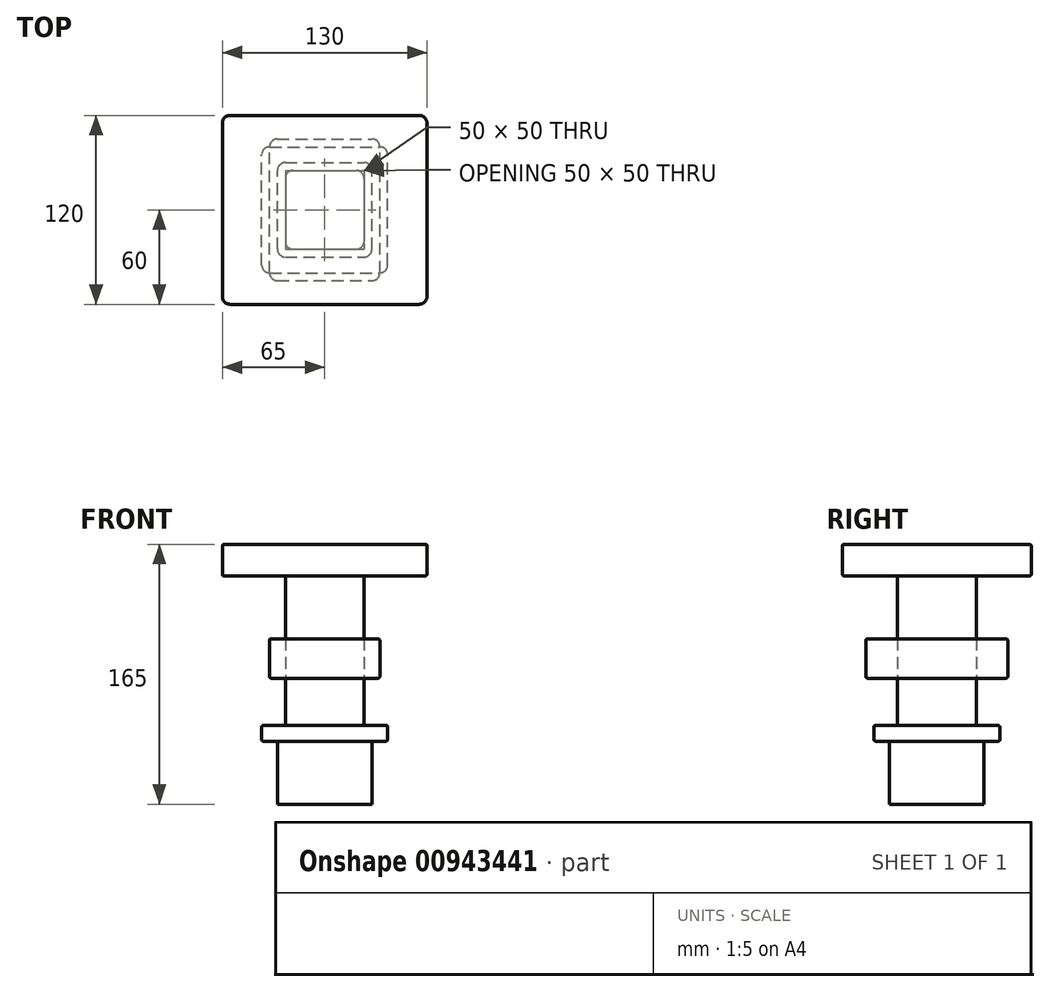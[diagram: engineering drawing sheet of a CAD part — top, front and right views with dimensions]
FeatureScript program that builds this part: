
annotation { "Feature Type Name" : "Feature", "Feature Type Description" : "" }
export const myFeature = defineFeature(function(context is Context, id is Id, definition is map)
    precondition{}
    {
        {
            var Q0;
            Q0=qCreatedBy(makeId("Top.planeOp"),FACE);
            var sketch = newSketch(context, id + "F0", { "sketchPlane" : qUnion([Q0])});
            skLineSegment(sketch, "E0.bottom", {"start": v(-30, -30) * mm, "end": v(30, -30) * mm});
            skLineSegment(sketch, "E0.top", {"start": v(-30, 30) * mm, "end": v(30, 30) * mm});
            skLineSegment(sketch, "E0.left", {"start": v(-30, -30) * mm, "end": v(-30, 30) * mm});
            skLineSegment(sketch, "E0.right", {"start": v(30, -30) * mm, "end": v(30, 30) * mm});
            skPoint(sketch, "E0.middle", {"position": v(0, 0) * mm});
            skSolve(sketch);
        }
        {
            var Q0;
            Q0=makeQuery(id+"F0.imprint","IMPRINT",FACE,{"disambiguationData":[TD([[makeQuery(id+"F0.imprint","IMPRINT",EDGE,{"derivedFrom":sQuery(id+"F0.wireOp",EDGE,"E0.bottom")}),1.0]])]});
            extrude(context, id + "F1", {"entities" : qUnion([Q0]), "depth" : 40 * mm, "offsetDistance" : 25 * mm});
        }
        {
            var Q0;
            Q0=makeQuery(id+"F1.opExtrude","CAP_FACE",FACE,{"disambiguationData":[OSD([sQuery(id+"F0.wireOp",EDGE,"E0.bottom"),sQuery(id+"F0.wireOp",EDGE,"E0.top"),sQuery(id+"F0.wireOp",EDGE,"E0.left"),sQuery(id+"F0.wireOp",EDGE,"E0.right")])],"isStart":false});
            var sketch = newSketch(context, id + "F2", { "sketchPlane" : qUnion([Q0])});
            skLineSegment(sketch, "E1.bottom", {"start": v(-40, -40) * mm, "end": v(40, -40) * mm});
            skLineSegment(sketch, "E1.top", {"start": v(-40, 40) * mm, "end": v(40, 40) * mm});
            skLineSegment(sketch, "E1.left", {"start": v(-40, -40) * mm, "end": v(-40, 40) * mm});
            skLineSegment(sketch, "E1.right", {"start": v(40, -40) * mm, "end": v(40, 40) * mm});
            skPoint(sketch, "E1.middle", {"position": v(0, 0) * mm});
            skSolve(sketch);
        }
        {
            var Q0;
            Q0 = qSketchRegion(id + "F2", true);
            extrude(context, id + "F3", {"entities" : qUnion([Q0]), "operationType" : NewBodyOperationType.ADD, "depth" : 10 * mm, "offsetDistance" : 25 * mm});
        }
        {
            var Q0;
            Q0=makeQuery(id+"F3.opExtrude","CAP_FACE",FACE,{"disambiguationData":[OSD([sQuery(id+"F2.wireOp",EDGE,"E1.bottom"),sQuery(id+"F2.wireOp",EDGE,"E1.top"),sQuery(id+"F2.wireOp",EDGE,"E1.left"),sQuery(id+"F2.wireOp",EDGE,"E1.right")])],"isStart":false});
            var sketch = newSketch(context, id + "F4", { "sketchPlane" : qUnion([Q0])});
            skLineSegment(sketch, "E2.bottom", {"start": v(-25, 25) * mm, "end": v(25, 25) * mm});
            skLineSegment(sketch, "E2.top", {"start": v(-25, -25) * mm, "end": v(25, -25) * mm});
            skLineSegment(sketch, "E2.left", {"start": v(-25, 25) * mm, "end": v(-25, -25) * mm});
            skLineSegment(sketch, "E2.right", {"start": v(25, 25) * mm, "end": v(25, -25) * mm});
            skPoint(sketch, "E2.middle", {"position": v(0, 0) * mm});
            skSolve(sketch);
        }
        {
            var Q0;
            Q0=makeQuery(id+"F4.imprint","IMPRINT",FACE,{"disambiguationData":[TD([[makeQuery(id+"F4.imprint","IMPRINT",EDGE,{"derivedFrom":sQuery(id+"F4.wireOp",EDGE,"E2.bottom")}),-1.0]])]});
            extrude(context, id + "F5", {"entities" : qUnion([Q0]), "operationType" : NewBodyOperationType.ADD, "depth" : 30 * mm, "offsetDistance" : 25 * mm});
        }
        {
            var Q0;
            Q0=makeQuery(id+"F5.opExtrude","CAP_FACE",FACE,{"disambiguationData":[OSD([sQuery(id+"F4.wireOp",EDGE,"E2.bottom"),sQuery(id+"F4.wireOp",EDGE,"E2.top"),sQuery(id+"F4.wireOp",EDGE,"E2.left"),sQuery(id+"F4.wireOp",EDGE,"E2.right")])],"isStart":false});
            var sketch = newSketch(context, id + "F6", { "sketchPlane" : qUnion([Q0])});
            skLineSegment(sketch, "E3.bottom", {"start": v(-35, -45) * mm, "end": v(35, -45) * mm});
            skLineSegment(sketch, "E3.top", {"start": v(-35, 45) * mm, "end": v(35, 45) * mm});
            skLineSegment(sketch, "E3.left", {"start": v(-35, -45) * mm, "end": v(-35, 45) * mm});
            skLineSegment(sketch, "E3.right", {"start": v(35, -45) * mm, "end": v(35, 45) * mm});
            skPoint(sketch, "E3.middle", {"position": v(0, 0) * mm});
            skSolve(sketch);
        }
        {
            var Q0;
            Q0=makeQuery(id+"F6.imprint","IMPRINT",FACE,{"disambiguationData":[TD([[makeQuery(id+"F6.imprint","IMPRINT",EDGE,{"derivedFrom":sQuery(id+"F6.wireOp",EDGE,"E3.bottom")}),1.0]])]});
            extrude(context, id + "F7", {"entities" : qUnion([Q0]), "depth" : 25 * mm, "offsetDistance" : 25 * mm});
        }
        {
            var Q0;
            Q0=makeQuery(id+"F5.opExtrude","CAP_FACE",FACE,{"disambiguationData":[OSD([sQuery(id+"F4.wireOp",EDGE,"E2.bottom"),sQuery(id+"F4.wireOp",EDGE,"E2.top"),sQuery(id+"F4.wireOp",EDGE,"E2.left"),sQuery(id+"F4.wireOp",EDGE,"E2.right")])],"isStart":false});
            extrude(context, id + "F8", {"entities" : qUnion([Q0]), "depth" : 65 * mm, "offsetDistance" : 25 * mm});
        }
        {
            var Q0;
            Q0=makeQuery(id+"F8.opExtrude","CAP_FACE",FACE,{"disambiguationData":[OSD([sQuery(id+"F4.wireOp",EDGE,"E2.bottom"),sQuery(id+"F4.wireOp",EDGE,"E2.top"),sQuery(id+"F4.wireOp",EDGE,"E2.left"),sQuery(id+"F4.wireOp",EDGE,"E2.right")])],"isStart":false});
            var sketch = newSketch(context, id + "F9", { "sketchPlane" : qUnion([Q0])});
            skLineSegment(sketch, "E4.bottom", {"start": v(-65, -60) * mm, "end": v(65, -60) * mm});
            skLineSegment(sketch, "E4.top", {"start": v(-65, 60) * mm, "end": v(65, 60) * mm});
            skLineSegment(sketch, "E4.left", {"start": v(-65, -60) * mm, "end": v(-65, 60) * mm});
            skLineSegment(sketch, "E4.right", {"start": v(65, -60) * mm, "end": v(65, 60) * mm});
            skPoint(sketch, "E4.middle", {"position": v(0, 0) * mm});
            skSolve(sketch);
        }
        {
            var Q0;
            Q0=makeQuery(id+"F9.imprint","IMPRINT",FACE,{"disambiguationData":[TD([[makeQuery(id+"F9.imprint","IMPRINT",EDGE,{"derivedFrom":sQuery(id+"F9.wireOp",EDGE,"E4.bottom")}),1.0]])]});
            var Q1;
            Q1=makeQuery(id+"F9.imprint","IMPRINT",FACE,{"disambiguationData":[TD([[makeQuery(id+"F9.imprint","IMPRINT",EDGE,{"derivedFrom":makeQuery(id+"F8.opExtrude","CAP_EDGE",EDGE,{"disambiguationData":[OSD([sQuery(id+"F4.wireOp",EDGE,"E2.bottom")])],"isStart":false})}),-1.0]])]});
            extrude(context, id + "F10", {"entities" : qUnion([Q0, Q1]), "operationType" : NewBodyOperationType.ADD, "depth" : 20 * mm, "offsetDistance" : 25 * mm});
        }
        {
            var Q0;
            Q0=makeQuery(id+"F1.opExtrude","SWEPT_FACE",FACE,{"disambiguationData":[OSD([sQuery(id+"F0.wireOp",EDGE,"E0.bottom")])]});
            var sketch = newSketch(context, id + "F11", { "sketchPlane" : qUnion([Q0])});
            skLineSegment(sketch, "E5.bottom", {"start": v(-10, 10.82) * mm, "end": v(10, 10.82) * mm});
            skLineSegment(sketch, "E5.top", {"start": v(-10, 30.82) * mm, "end": v(10, 30.82) * mm});
            skLineSegment(sketch, "E5.left", {"start": v(-10, 10.82) * mm, "end": v(-10, 30.82) * mm});
            skLineSegment(sketch, "E5.right", {"start": v(10, 10.82) * mm, "end": v(10, 30.82) * mm});
            skPoint(sketch, "E5.middle", {"position": v(0, 20.82) * mm});
            skSolve(sketch);
        }
        {
            var Q0;
            Q0 = qSketchRegion(id + "F11", true);
            extrude(context, id + "F12", {"entities" : qUnion([Q0]), "operationType" : NewBodyOperationType.ADD, "oppositeDirection" : true, "depth" : 60 * mm, "offsetDistance" : 25 * mm});
        }
        {
            var Q0;
            Q0=makeQuery(id+"F10.opExtrude","CAP_EDGE",EDGE,{"disambiguationData":[OSD([sQuery(id+"F9.wireOp",EDGE,"E4.left")])],"isStart":false});
            var Q1;
            Q1=makeQuery(id+"F10.opExtrude","CAP_EDGE",EDGE,{"disambiguationData":[OSD([sQuery(id+"F9.wireOp",EDGE,"E4.top")])],"isStart":false});
            var Q2;
            Q2=makeQuery(id+"F10.opExtrude","CAP_EDGE",EDGE,{"disambiguationData":[OSD([sQuery(id+"F9.wireOp",EDGE,"E4.right")])],"isStart":false});
            var Q3;
            Q3=makeQuery(id+"F10.opExtrude","CAP_EDGE",EDGE,{"disambiguationData":[OSD([sQuery(id+"F9.wireOp",EDGE,"E4.bottom")])],"isStart":false});
            var Q4;
            Q4=makeQuery(id+"F7.opExtrude","CAP_EDGE",EDGE,{"disambiguationData":[OSD([sQuery(id+"F6.wireOp",EDGE,"E3.left")])],"isStart":false});
            var Q5;
            Q5=makeQuery(id+"F7.opExtrude","CAP_EDGE",EDGE,{"disambiguationData":[OSD([sQuery(id+"F6.wireOp",EDGE,"E3.top")])],"isStart":false});
            var Q6;
            Q6=makeQuery(id+"F7.opExtrude","CAP_EDGE",EDGE,{"disambiguationData":[OSD([sQuery(id+"F6.wireOp",EDGE,"E3.bottom")])],"isStart":false});
            var Q7;
            Q7=makeQuery(id+"F7.opExtrude","CAP_EDGE",EDGE,{"disambiguationData":[OSD([sQuery(id+"F6.wireOp",EDGE,"E3.right")])],"isStart":false});
            var Q8;
            Q8=makeQuery(id+"F3.opExtrude","CAP_EDGE",EDGE,{"disambiguationData":[OSD([sQuery(id+"F2.wireOp",EDGE,"E1.left")])],"isStart":false});
            var Q9;
            Q9=makeQuery(id+"F3.opExtrude","CAP_EDGE",EDGE,{"disambiguationData":[OSD([sQuery(id+"F2.wireOp",EDGE,"E1.top")])],"isStart":false});
            var Q10;
            Q10=makeQuery(id+"F3.opExtrude","CAP_EDGE",EDGE,{"disambiguationData":[OSD([sQuery(id+"F2.wireOp",EDGE,"E1.right")])],"isStart":false});
            var Q11;
            Q11=makeQuery(id+"F3.opExtrude","CAP_EDGE",EDGE,{"disambiguationData":[OSD([sQuery(id+"F2.wireOp",EDGE,"E1.bottom")])],"isStart":false});
            var Q12;
            Q12=makeQuery(id+"F7.opExtrude","CAP_EDGE",EDGE,{"disambiguationData":[OSD([sQuery(id+"F6.wireOp",EDGE,"E3.left")])],"isStart":true});
            var Q13;
            Q13=makeQuery(id+"F7.opExtrude","CAP_EDGE",EDGE,{"disambiguationData":[OSD([sQuery(id+"F6.wireOp",EDGE,"E3.top")])],"isStart":true});
            var Q14;
            Q14=makeQuery(id+"F7.opExtrude","CAP_EDGE",EDGE,{"disambiguationData":[OSD([sQuery(id+"F6.wireOp",EDGE,"E3.bottom")])],"isStart":true});
            var Q15;
            Q15=makeQuery(id+"F7.opExtrude","CAP_EDGE",EDGE,{"disambiguationData":[OSD([sQuery(id+"F6.wireOp",EDGE,"E3.right")])],"isStart":true});
            var Q16;
            Q16=makeQuery(id+"F3.opExtrude","CAP_EDGE",EDGE,{"disambiguationData":[OSD([sQuery(id+"F2.wireOp",EDGE,"E1.right")])],"isStart":true});
            var Q17;
            Q17=makeQuery(id+"F3.opExtrude","CAP_EDGE",EDGE,{"disambiguationData":[OSD([sQuery(id+"F2.wireOp",EDGE,"E1.top")])],"isStart":true});
            var Q18;
            Q18=makeQuery(id+"F3.opExtrude","CAP_EDGE",EDGE,{"disambiguationData":[OSD([sQuery(id+"F2.wireOp",EDGE,"E1.left")])],"isStart":true});
            var Q19;
            Q19=makeQuery(id+"F3.opExtrude","CAP_EDGE",EDGE,{"disambiguationData":[OSD([sQuery(id+"F2.wireOp",EDGE,"E1.bottom")])],"isStart":true});
            var Q20;
            Q20=makeQuery(id+"F10.opExtrude","CAP_EDGE",EDGE,{"disambiguationData":[OSD([sQuery(id+"F9.wireOp",EDGE,"E4.bottom")])],"isStart":true});
            var Q21;
            Q21=makeQuery(id+"F10.opExtrude","CAP_EDGE",EDGE,{"disambiguationData":[OSD([sQuery(id+"F9.wireOp",EDGE,"E4.left")])],"isStart":true});
            var Q22;
            Q22=makeQuery(id+"F10.opExtrude","CAP_EDGE",EDGE,{"disambiguationData":[OSD([sQuery(id+"F9.wireOp",EDGE,"E4.right")])],"isStart":true});
            var Q23;
            Q23=makeQuery(id+"F10.opExtrude","CAP_EDGE",EDGE,{"disambiguationData":[OSD([sQuery(id+"F9.wireOp",EDGE,"E4.top")])],"isStart":true});
            fillet(context, id + "F13", {"entities" : qUnion([Q0, Q1, Q2, Q3, Q4, Q5, Q6, Q7, Q8, Q9, Q10, Q11, Q12, Q13, Q14, Q15, Q16, Q17, Q18, Q19, Q20, Q21, Q22, Q23]), "radius" : 1 * mm, "tangentPropagation" : true, "allowEdgeOverflow" : false});
        }
        {
            var Q0;
            Q0=makeQuery(id+"F8.opExtrude","SWEPT_EDGE",EDGE,{"disambiguationData":[OSD([sQuery(id+"F4.wireOp",EDGE,"E2.top"),sQuery(id+"F4.wireOp",EDGE,"E2.left")])]});
            var Q1;
            Q1=makeQuery(id+"F8.opExtrude","SWEPT_EDGE",EDGE,{"disambiguationData":[OSD([sQuery(id+"F4.wireOp",EDGE,"E2.bottom"),sQuery(id+"F4.wireOp",EDGE,"E2.left")])]});
            var Q2;
            Q2=makeQuery(id+"F8.opExtrude","SWEPT_EDGE",EDGE,{"disambiguationData":[OSD([sQuery(id+"F4.wireOp",EDGE,"E2.bottom"),sQuery(id+"F4.wireOp",EDGE,"E2.right")])]});
            var Q3;
            Q3=makeQuery(id+"F8.opExtrude","SWEPT_EDGE",EDGE,{"disambiguationData":[OSD([sQuery(id+"F4.wireOp",EDGE,"E2.top"),sQuery(id+"F4.wireOp",EDGE,"E2.right")])]});
            var Q4;
            Q4=makeQuery(id+"F1.opExtrude","SWEPT_EDGE",EDGE,{"disambiguationData":[OSD([sQuery(id+"F0.wireOp",EDGE,"E0.top"),sQuery(id+"F0.wireOp",EDGE,"E0.left")])]});
            var Q5;
            Q5=makeQuery(id+"F1.opExtrude","SWEPT_EDGE",EDGE,{"disambiguationData":[OSD([sQuery(id+"F0.wireOp",EDGE,"E0.bottom"),sQuery(id+"F0.wireOp",EDGE,"E0.right")])]});
            var Q6;
            Q6=makeQuery(id+"F1.opExtrude","SWEPT_EDGE",EDGE,{"disambiguationData":[OSD([sQuery(id+"F0.wireOp",EDGE,"E0.top"),sQuery(id+"F0.wireOp",EDGE,"E0.right")])]});
            var Q7;
            Q7=makeQuery(id+"F1.opExtrude","SWEPT_EDGE",EDGE,{"disambiguationData":[OSD([sQuery(id+"F0.wireOp",EDGE,"E0.bottom"),sQuery(id+"F0.wireOp",EDGE,"E0.left")])]});
            var Q8;
            Q8=makeQuery(id+"F5.opExtrude","SWEPT_EDGE",EDGE,{"disambiguationData":[OSD([sQuery(id+"F4.wireOp",EDGE,"E2.top"),sQuery(id+"F4.wireOp",EDGE,"E2.right")])]});
            var Q9;
            Q9=makeQuery(id+"F5.opExtrude","SWEPT_EDGE",EDGE,{"disambiguationData":[OSD([sQuery(id+"F4.wireOp",EDGE,"E2.bottom"),sQuery(id+"F4.wireOp",EDGE,"E2.left")])]});
            var Q10;
            Q10=makeQuery(id+"F5.opExtrude","SWEPT_EDGE",EDGE,{"disambiguationData":[OSD([sQuery(id+"F4.wireOp",EDGE,"E2.bottom"),sQuery(id+"F4.wireOp",EDGE,"E2.right")])]});
            var Q11;
            Q11=makeQuery(id+"F5.opExtrude","SWEPT_EDGE",EDGE,{"disambiguationData":[OSD([sQuery(id+"F4.wireOp",EDGE,"E2.top"),sQuery(id+"F4.wireOp",EDGE,"E2.left")])]});
            var Q12;
            Q12=makeQuery(id+"F3.opExtrude","SWEPT_EDGE",EDGE,{"disambiguationData":[OSD([sQuery(id+"F2.wireOp",EDGE,"E1.bottom"),sQuery(id+"F2.wireOp",EDGE,"E1.right")])]});
            var Q13;
            Q13=makeQuery(id+"F3.opExtrude","SWEPT_EDGE",EDGE,{"disambiguationData":[OSD([sQuery(id+"F2.wireOp",EDGE,"E1.top"),sQuery(id+"F2.wireOp",EDGE,"E1.right")])]});
            var Q14;
            Q14=makeQuery(id+"F7.opExtrude","SWEPT_EDGE",EDGE,{"disambiguationData":[OSD([sQuery(id+"F6.wireOp",EDGE,"E3.top"),sQuery(id+"F6.wireOp",EDGE,"E3.right")])]});
            var Q15;
            Q15=makeQuery(id+"F7.opExtrude","SWEPT_EDGE",EDGE,{"disambiguationData":[OSD([sQuery(id+"F6.wireOp",EDGE,"E3.bottom"),sQuery(id+"F6.wireOp",EDGE,"E3.right")])]});
            var Q16;
            Q16=makeQuery(id+"F10.opExtrude","SWEPT_EDGE",EDGE,{"disambiguationData":[OSD([sQuery(id+"F9.wireOp",EDGE,"E4.bottom"),sQuery(id+"F9.wireOp",EDGE,"E4.right")])]});
            var Q17;
            Q17=makeQuery(id+"F10.opExtrude","SWEPT_EDGE",EDGE,{"disambiguationData":[OSD([sQuery(id+"F9.wireOp",EDGE,"E4.top"),sQuery(id+"F9.wireOp",EDGE,"E4.right")])]});
            var Q18;
            Q18=makeQuery(id+"F7.opExtrude","SWEPT_EDGE",EDGE,{"disambiguationData":[OSD([sQuery(id+"F6.wireOp",EDGE,"E3.top"),sQuery(id+"F6.wireOp",EDGE,"E3.left")])]});
            var Q19;
            Q19=makeQuery(id+"F3.opExtrude","SWEPT_EDGE",EDGE,{"disambiguationData":[OSD([sQuery(id+"F2.wireOp",EDGE,"E1.top"),sQuery(id+"F2.wireOp",EDGE,"E1.left")])]});
            var Q20;
            Q20=makeQuery(id+"F3.opExtrude","SWEPT_EDGE",EDGE,{"disambiguationData":[OSD([sQuery(id+"F2.wireOp",EDGE,"E1.bottom"),sQuery(id+"F2.wireOp",EDGE,"E1.left")])]});
            var Q21;
            Q21=makeQuery(id+"F7.opExtrude","SWEPT_EDGE",EDGE,{"disambiguationData":[OSD([sQuery(id+"F6.wireOp",EDGE,"E3.bottom"),sQuery(id+"F6.wireOp",EDGE,"E3.left")])]});
            var Q22;
            Q22=makeQuery(id+"F10.opExtrude","SWEPT_EDGE",EDGE,{"disambiguationData":[OSD([sQuery(id+"F9.wireOp",EDGE,"E4.bottom"),sQuery(id+"F9.wireOp",EDGE,"E4.left")])]});
            var Q23;
            Q23=makeQuery(id+"F10.opExtrude","SWEPT_EDGE",EDGE,{"disambiguationData":[OSD([sQuery(id+"F9.wireOp",EDGE,"E4.top"),sQuery(id+"F9.wireOp",EDGE,"E4.left")])]});
            fillet(context, id + "F14", {"entities" : qUnion([Q0, Q1, Q2, Q3, Q4, Q5, Q6, Q7, Q8, Q9, Q10, Q11, Q12, Q13, Q14, Q15, Q16, Q17, Q18, Q19, Q20, Q21, Q22, Q23]), "radius" : 5 * mm, "tangentPropagation" : true, "allowEdgeOverflow" : false});
        }
    });
